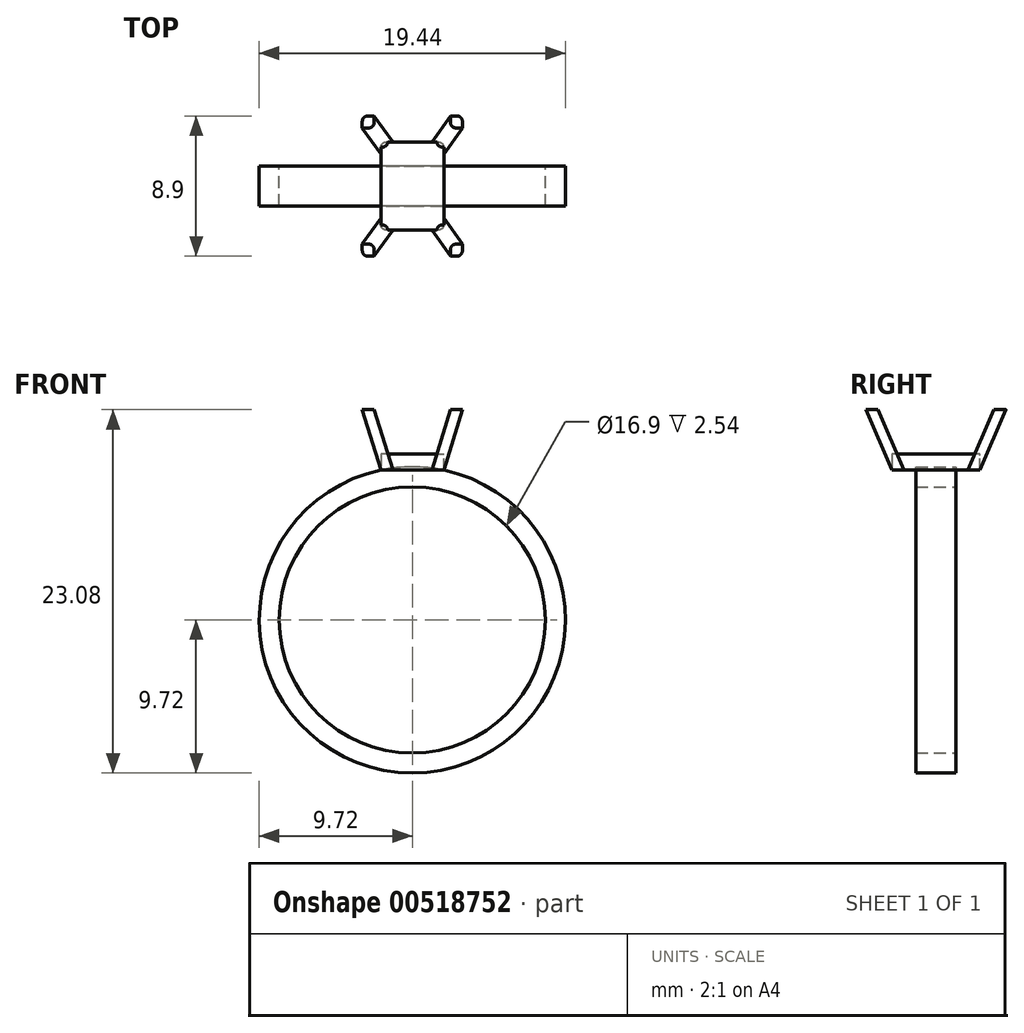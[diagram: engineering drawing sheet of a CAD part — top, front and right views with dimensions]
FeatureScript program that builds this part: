
annotation { "Feature Type Name" : "Feature", "Feature Type Description" : "" }
export const myFeature = defineFeature(function(context is Context, id is Id, definition is map)
    precondition{}
    {
        {
            var Q0;
            Q0=qCreatedBy(makeId("Front.planeOp"),FACE);
            var sketch = newSketch(context, id + "F0", { "sketchPlane" : qUnion([Q0])});
            skCircle(sketch, "E0", {"center": v(0, 0) * mm, "radius": 8.45 * mm});
            skCircle(sketch, "E1", {"center": v(0, 0) * mm, "radius": 9.72 * mm});
            skSolve(sketch);
        }
        {
            var Q0;
            Q0=makeQuery(id+"F0.imprint","IMPRINT",FACE,{"disambiguationData":[TD([[makeQuery(id+"F0.imprint","IMPRINT",EDGE,{"derivedFrom":sQuery(id+"F0.wireOp",EDGE,"E0")}),-1.0]])]});
            extrude(context, id + "F1", {"entities" : qUnion([Q0]), "endBound" : BoundingType.SYMMETRIC, "depth" : 2.54 * mm, "offsetDistance" : 25.4 * mm});
        }
        {
            var Q0;
            Q0=qCreatedBy(makeId("Front.planeOp"),FACE);
            var sketch = newSketch(context, id + "F2", { "sketchPlane" : qUnion([Q0])});
            skLineSegment(sketch, "E2", {"start": v(0, 0) * mm, "end": v(0, 8.45) * mm, "construction": true});
            skLineSegment(sketch, "E3.bottom", {"start": v(2, 10.53) * mm, "end": v(-2, 10.53) * mm});
            skLineSegment(sketch, "E3.top", {"start": v(2, 9.51) * mm, "end": v(-2, 9.51) * mm});
            skLineSegment(sketch, "E3.left", {"start": v(2, 10.53) * mm, "end": v(2, 9.51) * mm});
            skLineSegment(sketch, "E3.right", {"start": v(-2, 10.53) * mm, "end": v(-2, 9.51) * mm});
            skSolve(sketch);
        }
        {
            var Q0;
            Q0 = qSketchRegion(id + "F2", true);
            var Q1;
            Q1 = qConstructionFilter(qBodyType(qCreatedBy(id + "F2" ,EDGE), BodyType.WIRE), ConstructionObject.NO);
            extrude(context, id + "F3", {"entities" : qUnion([Q0]), "surfaceEntities" : qUnion([Q1]), "endBound" : BoundingType.SYMMETRIC, "depth" : 5.6 * mm, "offsetDistance" : 25.4 * mm});
        }
        {
            var Q0;
            Q0=qCreatedBy(makeId("Origin.pointOp"),VERTEX);
            var Q1;
            Q1=makeQuery(id+"F3.opExtrude","CAP_VERTEX",VERTEX,{"disambiguationData":[OSD([sQuery(id+"F2.wireOp",EDGE,"E3.top"),sQuery(id+"F2.wireOp",EDGE,"E3.left")])],"isStart":true});
            var Q2;
            Q2=makeQuery(id+"F3.opExtrude","CAP_VERTEX",VERTEX,{"disambiguationData":[OSD([sQuery(id+"F2.wireOp",EDGE,"E3.top"),sQuery(id+"F2.wireOp",EDGE,"E3.right")])],"isStart":false});
            cPlane(context, id + "F4", {"entities" : qUnion([Q0, Q1, Q2]), "cplaneType" : CPlaneType.THREE_POINT, "offset" : 25.4 * mm, "width" : 152.4 * mm, "height" : 152.4 * mm});
        }
        {
            var Q0;
            Q0=makeQuery(id+"F3.opExtrude","SWEPT_FACE",FACE,{"disambiguationData":[OSD([sQuery(id+"F2.wireOp",EDGE,"E3.top")])]});
            var sketch = newSketch(context, id + "F5", { "sketchPlane" : qUnion([Q0])});
            skLineSegment(sketch, "E4.bottom", {"start": v(2, -2.8) * mm, "end": v(1.24, -2.8) * mm});
            skLineSegment(sketch, "E4.top", {"start": v(2, -2.04) * mm, "end": v(1.24, -2.04) * mm});
            skLineSegment(sketch, "E4.left", {"start": v(2, -2.8) * mm, "end": v(2, -2.04) * mm});
            skLineSegment(sketch, "E4.right", {"start": v(1.24, -2.8) * mm, "end": v(1.24, -2.04) * mm});
            skSolve(sketch);
        }
        {
            var Q0;
            Q0=qCreatedBy(id+"F4.planeOp",FACE);
            var sketch = newSketch(context, id + "F6", { "sketchPlane" : qUnion([Q0])});
            skLineSegment(sketch, "E5", {"start": v(-3.44, 9.51) * mm, "end": v(-5.47, 13.36) * mm});
            skSolve(sketch);
        }
        {
            var Q0;
            Q0 = qSketchRegion(id + "F5", true);
            var Q1;
            Q1 = qConstructionFilter(qBodyType(qCreatedBy(id + "F6" ,EDGE), BodyType.WIRE), ConstructionObject.NO);
            sweep(context, id + "F7", {"operationType" : NewBodyOperationType.ADD, "profiles" : qUnion([Q0]), "path" : qUnion([Q1])});
        }
        {
            var Q0;
            Q0=makeQuery(id+"F3.opExtrude","SWEPT_FACE",FACE,{"disambiguationData":[OSD([sQuery(id+"F2.wireOp",EDGE,"E3.top")])]});
            var sketch = newSketch(context, id + "F8", { "sketchPlane" : qUnion([Q0])});
            skLineSegment(sketch, "E6.bottom", {"start": v(-2, -2.8) * mm, "end": v(-1.24, -2.8) * mm});
            skLineSegment(sketch, "E6.top", {"start": v(-2, -2.04) * mm, "end": v(-1.24, -2.04) * mm});
            skLineSegment(sketch, "E6.left", {"start": v(-2, -2.8) * mm, "end": v(-2, -2.04) * mm});
            skLineSegment(sketch, "E6.right", {"start": v(-1.24, -2.8) * mm, "end": v(-1.24, -2.04) * mm});
            skSolve(sketch);
        }
        {
            var Q0;
            {var subQ3=sQuery(id+"F8.wireOp",EDGE,"E6.top");Q0=makeQuery(id+"F8.imprint","IMPRINT",FACE,{"disambiguationData":[TD([[makeQuery(id+"F8.imprint","IMPRINT",EDGE,{"derivedFrom":subQ3}),1.0]])]});}
            var sketch = newSketch(context, id + "F9", { "sketchPlane" : qUnion([Q0])});
            skLineSegment(sketch, "E7.bottom", {"start": v(-2, 2.8) * mm, "end": v(-1.24, 2.8) * mm});
            skLineSegment(sketch, "E7.top", {"start": v(-2, 2.04) * mm, "end": v(-1.24, 2.04) * mm});
            skLineSegment(sketch, "E7.left", {"start": v(-2, 2.8) * mm, "end": v(-2, 2.04) * mm});
            skLineSegment(sketch, "E7.right", {"start": v(-1.24, 2.8) * mm, "end": v(-1.24, 2.04) * mm});
            skSolve(sketch);
        }
        {
            var Q0;
            {var subQ3=sQuery(id+"F8.wireOp",EDGE,"E6.top");Q0=makeQuery(id+"F8.imprint","IMPRINT",FACE,{"disambiguationData":[TD([[makeQuery(id+"F8.imprint","IMPRINT",EDGE,{"derivedFrom":subQ3}),1.0]])]});}
            var sketch = newSketch(context, id + "F10", { "sketchPlane" : qUnion([Q0])});
            skLineSegment(sketch, "E8.bottom", {"start": v(2, 2.8) * mm, "end": v(1.24, 2.8) * mm});
            skLineSegment(sketch, "E8.top", {"start": v(2, 2.04) * mm, "end": v(1.24, 2.04) * mm});
            skLineSegment(sketch, "E8.left", {"start": v(2, 2.8) * mm, "end": v(2, 2.04) * mm});
            skLineSegment(sketch, "E8.right", {"start": v(1.24, 2.8) * mm, "end": v(1.24, 2.04) * mm});
            skSolve(sketch);
        }
        {
            var Q0;
            Q0=qCreatedBy(id+"F4.planeOp",FACE);
            var sketch = newSketch(context, id + "F11", { "sketchPlane" : qUnion([Q0])});
            skLineSegment(sketch, "E9", {"start": v(5.47, 13.36) * mm, "end": v(3.44, 9.51) * mm});
            skSolve(sketch);
        }
        {
            var Q0;
            Q0 = qSketchRegion(id + "F9", true);
            var Q1;
            Q1 = qConstructionFilter(qBodyType(qCreatedBy(id + "F11" ,EDGE), BodyType.WIRE), ConstructionObject.NO);
            sweep(context, id + "F12", {"operationType" : NewBodyOperationType.ADD, "profiles" : qUnion([Q0]), "path" : qUnion([Q1])});
        }
        {
            var Q0;
            Q0=sQuery(id+"F10.wireOp",VERTEX,"E8.bottom.start");
            var Q1;
            Q1=qCreatedBy(makeId("Origin.pointOp"),VERTEX);
            var Q2;
            Q2=sQuery(id+"F8.wireOp",VERTEX,"E6.bottom.start");
            cPlane(context, id + "F13", {"entities" : qUnion([Q0, Q1, Q2]), "cplaneType" : CPlaneType.THREE_POINT, "offset" : 25.4 * mm, "width" : 152.4 * mm, "height" : 152.4 * mm});
        }
        {
            var Q0;
            Q0=qCreatedBy(id+"F13.planeOp",FACE);
            var sketch = newSketch(context, id + "F14", { "sketchPlane" : qUnion([Q0])});
            skLineSegment(sketch, "E10", {"start": v(3.44, 9.51) * mm, "end": v(5.47, 13.36) * mm});
            skSolve(sketch);
        }
        {
            var Q0;
            Q0 = qSketchRegion(id + "F10", true);
            var Q1;
            Q1 = qConstructionFilter(qBodyType(qCreatedBy(id + "F14" ,EDGE), BodyType.WIRE), ConstructionObject.NO);
            sweep(context, id + "F15", {"operationType" : NewBodyOperationType.ADD, "profiles" : qUnion([Q0]), "path" : qUnion([Q1])});
        }
        {
            var Q0;
            Q0=qCreatedBy(id+"F13.planeOp",FACE);
            var sketch = newSketch(context, id + "F16", { "sketchPlane" : qUnion([Q0])});
            skLineSegment(sketch, "E11", {"start": v(-5.47, 13.36) * mm, "end": v(-3.44, 9.51) * mm});
            skSolve(sketch);
        }
        {
            var Q0;
            Q0 = qSketchRegion(id + "F8", true);
            var Q1;
            Q1 = qConstructionFilter(qBodyType(qCreatedBy(id + "F16" ,EDGE), BodyType.WIRE), ConstructionObject.NO);
            sweep(context, id + "F17", {"operationType" : NewBodyOperationType.ADD, "profiles" : qUnion([Q0]), "path" : qUnion([Q1])});
        }
        {
            var Q0;
            Q0=makeQuery(id+"F12.opSweep","SWEPT_EDGE",EDGE,{"disambiguationData":[OSD([sQuery(id+"F9.wireOp",EDGE,"E7.top"),sQuery(id+"F9.wireOp",EDGE,"E7.right"),sQuery(id+"F11.wireOp",EDGE,"E9")])]});
            var Q1;
            Q1=makeQuery(id+"F7.opSweep","SWEPT_EDGE",EDGE,{"disambiguationData":[OSD([sQuery(id+"F5.wireOp",EDGE,"E4.top"),sQuery(id+"F5.wireOp",EDGE,"E4.right"),sQuery(id+"F6.wireOp",EDGE,"E5")])]});
            var Q2;
            Q2=makeQuery(id+"F12.opSweep","SWEPT_EDGE",EDGE,{"disambiguationData":[OSD([sQuery(id+"F9.wireOp",EDGE,"E7.bottom"),sQuery(id+"F9.wireOp",EDGE,"E7.left"),sQuery(id+"F11.wireOp",EDGE,"E9")])]});
            var Q3;
            Q3=makeQuery(id+"F7.opSweep","SWEPT_EDGE",EDGE,{"disambiguationData":[OSD([sQuery(id+"F5.wireOp",EDGE,"E4.bottom"),sQuery(id+"F5.wireOp",EDGE,"E4.left"),sQuery(id+"F6.wireOp",EDGE,"E5")])]});
            var Q4;
            Q4=makeQuery(id+"F17.opSweep","SWEPT_EDGE",EDGE,{"disambiguationData":[OSD([sQuery(id+"F8.wireOp",EDGE,"E6.bottom"),sQuery(id+"F8.wireOp",EDGE,"E6.left"),sQuery(id+"F16.wireOp",EDGE,"E11")])]});
            var Q5;
            Q5=makeQuery(id+"F15.opSweep","SWEPT_EDGE",EDGE,{"disambiguationData":[OSD([sQuery(id+"F10.wireOp",EDGE,"E8.top"),sQuery(id+"F10.wireOp",EDGE,"E8.right"),sQuery(id+"F14.wireOp",EDGE,"E10")])]});
            var Q6;
            Q6=makeQuery(id+"F17.opSweep","SWEPT_EDGE",EDGE,{"disambiguationData":[OSD([sQuery(id+"F8.wireOp",EDGE,"E6.top"),sQuery(id+"F8.wireOp",EDGE,"E6.right"),sQuery(id+"F16.wireOp",EDGE,"E11")])]});
            var Q7;
            Q7=makeQuery(id+"F15.opSweep","SWEPT_EDGE",EDGE,{"disambiguationData":[OSD([sQuery(id+"F10.wireOp",EDGE,"E8.bottom"),sQuery(id+"F10.wireOp",EDGE,"E8.left"),sQuery(id+"F14.wireOp",EDGE,"E10")])]});
            fillet(context, id + "F18", {"entities" : qUnion([Q0, Q1, Q2, Q3, Q4, Q5, Q6, Q7]), "radius" : 0.38 * mm, "tangentPropagation" : true, "allowEdgeOverflow" : false});
        }
    });
